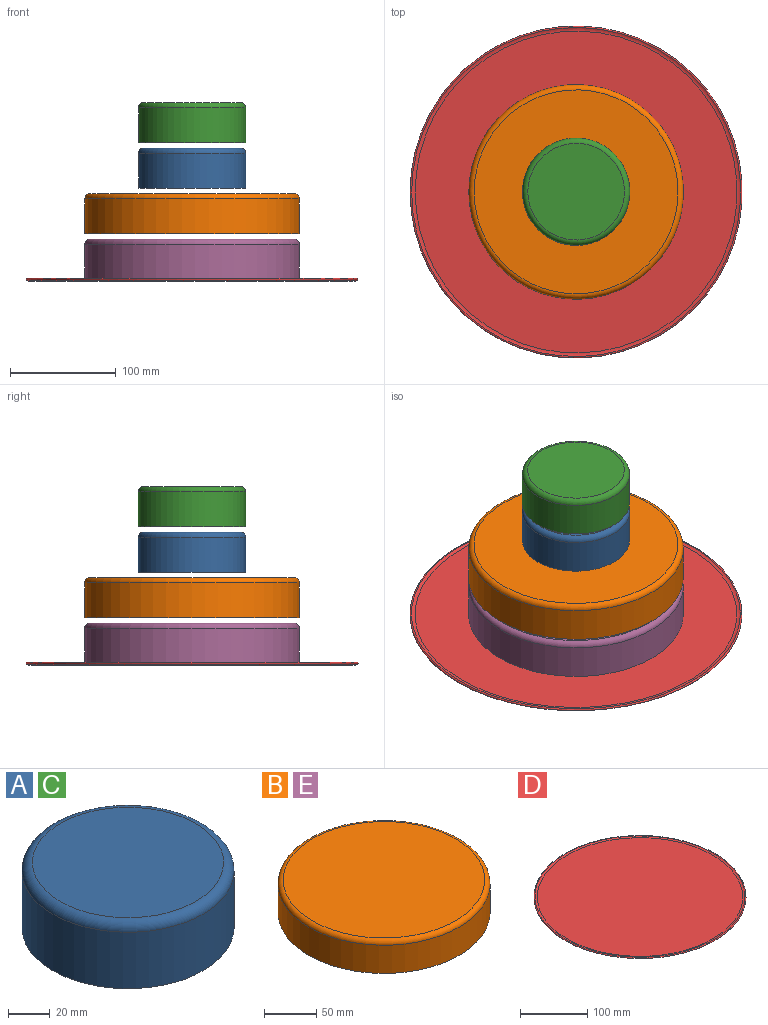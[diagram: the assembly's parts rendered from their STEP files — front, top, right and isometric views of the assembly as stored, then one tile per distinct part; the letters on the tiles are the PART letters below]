
ASSEMBLY  parts=5 mates=3
PART A: 4 faces, bbox 110x110x38.1 mm
  f0: plane 101.6x101.6mm, normal (0,0,-1), area 8107.3mm2, adj f1
  f1: cylinder r=50.8mm len=101.6mm, axis (0,0,-1), area 10565.1mm2, adj f0,f3
  f2: plane 91.6x91.6mm, normal (0,0,1), area 6589.9mm2, adj f3
  f3: torus R=45.8mm, axis (0,0,-1), area 2417.2mm2, adj f1,f2
PART B: 4 faces, bbox 219.9x219.9x38.1 mm
  f0: plane 203.2x203.2mm, normal (0,0,-1), area 32429.3mm2, adj f1
  f1: cylinder r=101.6mm len=203.2mm, axis (0,0,-1), area 21130.1mm2, adj f0,f3
  f2: plane 193.2x193.2mm, normal (0,0,1), area 29316mm2, adj f3
  f3: torus R=96.6mm, axis (0,0,-1), area 4924.1mm2, adj f1,f2
PART C: same geometry as A
PART D: 5 faces, bbox 343.7x343.7x4 mm
  f0: plane 304.8x304.8mm, normal (0,0,-1), area 72965.9mm2, adj f1
  f1: torus R=152.4mm, axis (0,0,-1), area 4418.8mm2, adj f0,f2
  f2: torus R=156.27mm, axis (0,0,-1), area 3095.7mm2, adj f1,f3
  f3: torus R=152.4mm, axis (0,0,-1), area 3425.9mm2, adj f2,f4
  f4: plane 304.8x304.8mm, normal (0,0,1), area 72965.9mm2, adj f3
PART E: same geometry as B
PLACE A t=(0,0,86.2)mm
PLACE B t=(0,0,43.1)mm
PLACE C t=(0,0,129.3)mm
PLACE D t=(0,0,-2)mm fixed
PLACE E at identity
MATE fastened E.f1 <-> B.f1  axis (0,0,1) through (0,0,38.1)mm
MATE fastened A.f1 <-> C.f1  axis (0,0,1) through (0,0,124.3)mm
MATE fastened B.f1 <-> A.f1  axis (0,0,1) through (0,0,81.2)mm
